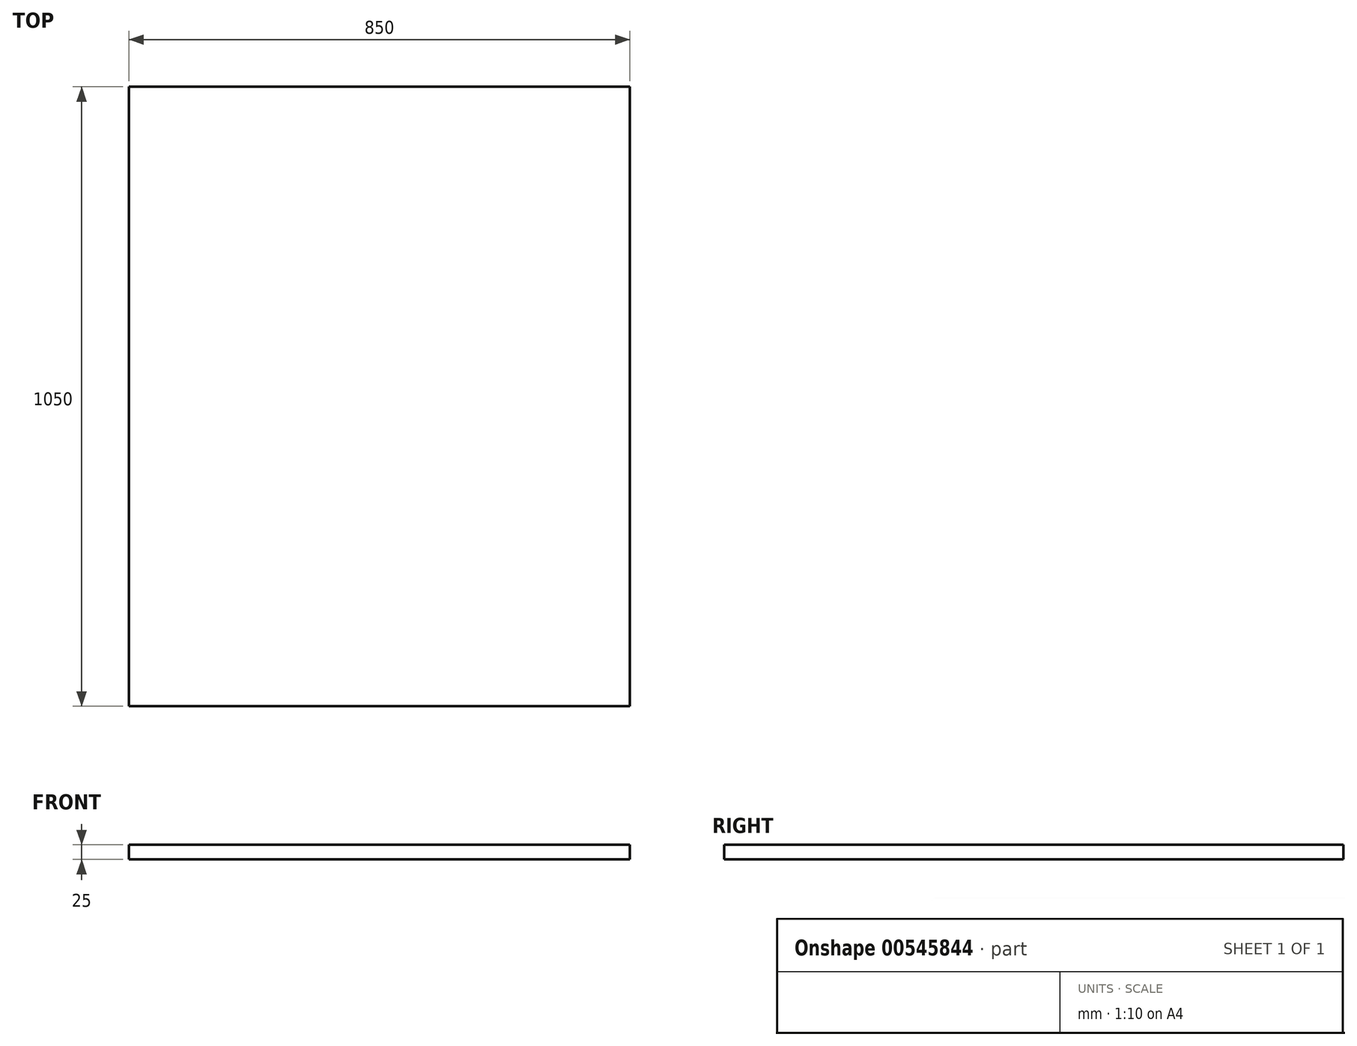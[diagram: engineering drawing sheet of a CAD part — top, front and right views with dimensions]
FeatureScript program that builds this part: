
annotation { "Feature Type Name" : "Feature", "Feature Type Description" : "" }
export const myFeature = defineFeature(function(context is Context, id is Id, definition is map)
    precondition{}
    {
        {
            var Q0;
            Q0=qCreatedBy(makeId("Top.planeOp"),FACE);
            var sketch = newSketch(context, id + "F0", { "sketchPlane" : qUnion([Q0])});
            skLineSegment(sketch, "E0", {"start": v(0, 850) * mm, "end": v(0, -850) * mm, "construction": true});
            skLineSegment(sketch, "E1", {"start": v(0, -850) * mm, "end": v(-425, -850) * mm, "construction": true});
            skLineSegment(sketch, "E2", {"start": v(-675, 850) * mm, "end": v(0, 850) * mm, "construction": true});
            skLineSegment(sketch, "E3", {"start": v(-675, -500) * mm, "end": v(-675, -850) * mm, "construction": true});
            skLineSegment(sketch, "E4", {"start": v(-675, -850) * mm, "end": v(-425, -850) * mm, "construction": true});
            skLineSegment(sketch, "E5.MirrorCS", {"start": v(675, 850) * mm, "end": v(0, 850) * mm, "construction": true});
            skLineSegment(sketch, "E6.MirrorCS", {"start": v(0, -850) * mm, "end": v(425, -850) * mm, "construction": true});
            skLineSegment(sketch, "E7", {"start": v(-425, -850) * mm, "end": v(-675, -500) * mm, "construction": true});
            skLineSegment(sketch, "E8", {"start": v(675, 850) * mm, "end": v(675, -500) * mm, "construction": true});
            skLineSegment(sketch, "E9", {"start": v(425, -850) * mm, "end": v(-425, -850) * mm});
            skLineSegment(sketch, "E10", {"start": v(675, -500) * mm, "end": v(425, -850) * mm, "construction": true});
            skLineSegment(sketch, "E11", {"start": v(-675, -500) * mm, "end": v(-675, 850) * mm, "construction": true});
            skLineSegment(sketch, "E12", {"start": v(-425, 200) * mm, "end": v(0, 200) * mm});
            skLineSegment(sketch, "E13.MirrorCS", {"start": v(425, 200) * mm, "end": v(0, 200) * mm});
            skLineSegment(sketch, "E14", {"start": v(-425, 200) * mm, "end": v(-425, -850) * mm});
            skLineSegment(sketch, "E15", {"start": v(425, 200) * mm, "end": v(425, -850) * mm});
            skSolve(sketch);
        }
        {
            var Q0;
            Q0=makeQuery(id+"F0.imprint","IMPRINT",FACE,{"disambiguationData":[TD([[makeQuery(id+"F0.imprint","IMPRINT",EDGE,{"derivedFrom":sQuery(id+"F0.wireOp",EDGE,"E9")}),-1.0]])]});
            extrude(context, id + "F1", {"entities" : qUnion([Q0]), "depth" : 25 * mm, "offsetDistance" : 25 * mm});
        }
    });
